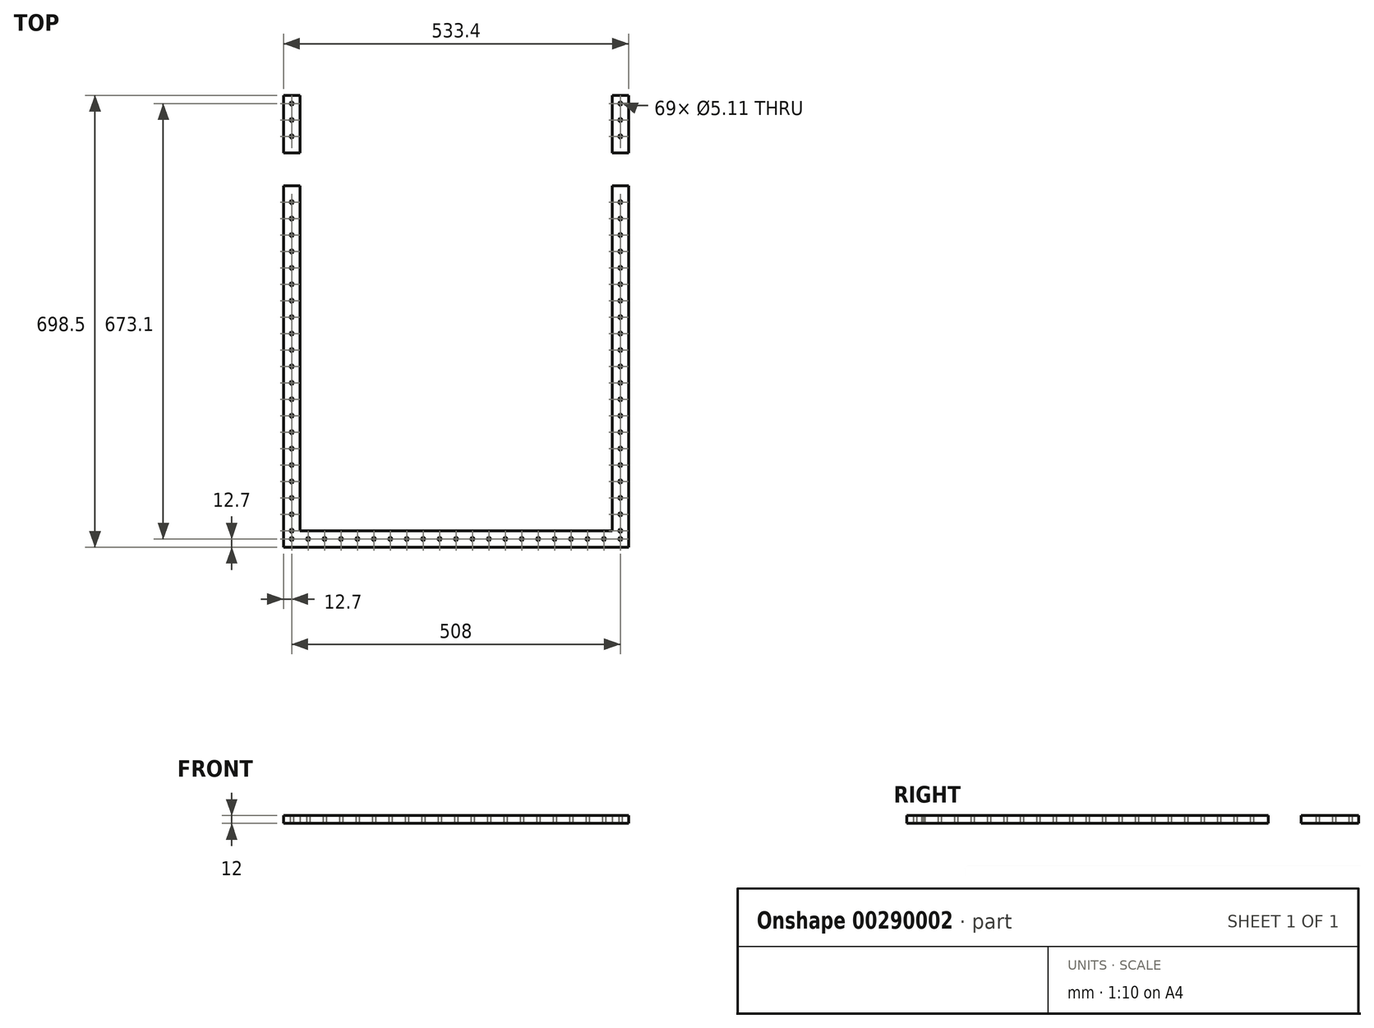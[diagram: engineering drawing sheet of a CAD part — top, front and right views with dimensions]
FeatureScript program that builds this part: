
annotation { "Feature Type Name" : "Feature", "Feature Type Description" : "" }
export const myFeature = defineFeature(function(context is Context, id is Id, definition is map)
    precondition{}
    {
        {
            var Q0;
            Q0=qCreatedBy(makeId("Top.planeOp"),FACE);
            var sketch = newSketch(context, id + "F0", { "sketchPlane" : qUnion([Q0])});
            skLineSegment(sketch, "E0.bottom", {"start": v(304.8, 0) * mm, "end": v(-304.8, 0) * mm, "construction": true});
            skLineSegment(sketch, "E0.top", {"start": v(304.8, 1066.8) * mm, "end": v(-304.8, 1066.8) * mm, "construction": true});
            skLineSegment(sketch, "E0.left", {"start": v(304.8, 0) * mm, "end": v(304.8, 1066.8) * mm, "construction": true});
            skLineSegment(sketch, "E0.right", {"start": v(-304.8, 0) * mm, "end": v(-304.8, 1066.8) * mm, "construction": true});
            skLineSegment(sketch, "E1.bottom", {"start": v(279.4, 965.2) * mm, "end": v(304.8, 965.2) * mm});
            skLineSegment(sketch, "E1.top", {"start": v(279.4, 914.4) * mm, "end": v(304.8, 914.4) * mm});
            skLineSegment(sketch, "E1.left", {"start": v(279.4, 965.2) * mm, "end": v(279.4, 914.4) * mm});
            skLineSegment(sketch, "E1.right", {"start": v(304.8, 965.2) * mm, "end": v(304.8, 914.4) * mm});
            skLineSegment(sketch, "E2.bottom", {"start": v(-279.4, 965.2) * mm, "end": v(-304.8, 965.2) * mm});
            skLineSegment(sketch, "E2.top", {"start": v(-279.4, 914.4) * mm, "end": v(-304.8, 914.4) * mm});
            skLineSegment(sketch, "E2.left", {"start": v(-279.4, 965.2) * mm, "end": v(-279.4, 914.4) * mm});
            skLineSegment(sketch, "E2.right", {"start": v(-304.8, 965.2) * mm, "end": v(-304.8, 914.4) * mm});
            skLineSegment(sketch, "E3.bottom", {"start": v(-214.63, 383.54) * mm, "end": v(214.63, 383.54) * mm, "construction": true});
            skLineSegment(sketch, "E3.top", {"start": v(-214.63, 1066.8) * mm, "end": v(214.63, 1066.8) * mm, "construction": true});
            skLineSegment(sketch, "E3.left", {"start": v(-214.63, 383.54) * mm, "end": v(-214.63, 1066.8) * mm, "construction": true});
            skLineSegment(sketch, "E3.right", {"start": v(214.63, 383.54) * mm, "end": v(214.63, 1066.8) * mm, "construction": true});
            skPoint(sketch, "E3.middle", {"position": v(0, 725.17) * mm});
            skLineSegment(sketch, "E4.bottom", {"start": v(25.4, 345.44) * mm, "end": v(-25.4, 345.44) * mm});
            skLineSegment(sketch, "E4.top", {"start": v(25.4, 320.04) * mm, "end": v(-25.4, 320.04) * mm});
            skLineSegment(sketch, "E4.left", {"start": v(25.4, 345.44) * mm, "end": v(25.4, 320.04) * mm});
            skLineSegment(sketch, "E4.right", {"start": v(-25.4, 345.44) * mm, "end": v(-25.4, 320.04) * mm});
            skPoint(sketch, "E4.middle", {"position": v(0, 332.74) * mm});
            skLineSegment(sketch, "E5", {"start": v(0, 1066.8) * mm, "end": v(0, 0) * mm, "construction": true});
            skLineSegment(sketch, "E6", {"start": v(-266.7, 1054.1) * mm, "end": v(-241.3, 1054.1) * mm});
            skLineSegment(sketch, "E7", {"start": v(-241.3, 1054.1) * mm, "end": v(-241.3, 965.2) * mm});
            skLineSegment(sketch, "E8", {"start": v(-266.7, 1054.1) * mm, "end": v(-266.7, 965.2) * mm});
            skLineSegment(sketch, "E9", {"start": v(-266.7, 914.4) * mm, "end": v(-266.7, 355.6) * mm});
            skLineSegment(sketch, "E10", {"start": v(-266.7, 355.6) * mm, "end": v(266.7, 355.6) * mm});
            skLineSegment(sketch, "E11", {"start": v(266.7, 355.6) * mm, "end": v(266.7, 914.4) * mm});
            skLineSegment(sketch, "E12", {"start": v(266.7, 965.2) * mm, "end": v(266.7, 1054.1) * mm});
            skLineSegment(sketch, "E13", {"start": v(266.7, 1054.1) * mm, "end": v(241.3, 1054.1) * mm});
            skLineSegment(sketch, "E14", {"start": v(241.3, 1054.1) * mm, "end": v(241.3, 965.2) * mm});
            skLineSegment(sketch, "E15", {"start": v(241.3, 914.4) * mm, "end": v(241.3, 381) * mm});
            skLineSegment(sketch, "E16", {"start": v(241.3, 381) * mm, "end": v(-241.3, 381) * mm});
            skLineSegment(sketch, "E17", {"start": v(-241.3, 914.4) * mm, "end": v(-241.3, 381) * mm});
            skPoint(sketch, "E17.startSnap0", {"position": v(-292.1, 914.4) * mm});
            skPoint(sketch, "E18", {"position": v(0, 355.6) * mm});
            skCircle(sketch, "E19", {"center": v(-254, 1041.4) * mm, "radius": 2.55 * mm});
            skCircle(sketch, "E20.0.1.0", {"center": v(-254, 1016) * mm, "radius": 2.55 * mm});
            skCircle(sketch, "E20.0.2.0", {"center": v(-254, 990.6) * mm, "radius": 2.55 * mm});
            skCircle(sketch, "E20.0.6.0", {"center": v(-254, 889) * mm, "radius": 2.55 * mm});
            skCircle(sketch, "E20.0.7.0", {"center": v(-254, 863.6) * mm, "radius": 2.55 * mm});
            skCircle(sketch, "E20.0.8.0", {"center": v(-254, 838.2) * mm, "radius": 2.55 * mm});
            skCircle(sketch, "E20.0.9.0", {"center": v(-254, 812.8) * mm, "radius": 2.55 * mm});
            skCircle(sketch, "E20.0.10.0", {"center": v(-254, 787.4) * mm, "radius": 2.55 * mm});
            skCircle(sketch, "E20.0.11.0", {"center": v(-254, 762) * mm, "radius": 2.55 * mm});
            skCircle(sketch, "E20.0.12.0", {"center": v(-254, 736.6) * mm, "radius": 2.55 * mm});
            skCircle(sketch, "E20.0.13.0", {"center": v(-254, 711.2) * mm, "radius": 2.55 * mm});
            skCircle(sketch, "E20.0.14.0", {"center": v(-254, 685.8) * mm, "radius": 2.55 * mm});
            skCircle(sketch, "E20.0.15.0", {"center": v(-254, 660.4) * mm, "radius": 2.55 * mm});
            skCircle(sketch, "E20.0.16.0", {"center": v(-254, 635) * mm, "radius": 2.55 * mm});
            skCircle(sketch, "E20.0.17.0", {"center": v(-254, 609.6) * mm, "radius": 2.55 * mm});
            skCircle(sketch, "E20.0.18.0", {"center": v(-254, 584.2) * mm, "radius": 2.55 * mm});
            skCircle(sketch, "E20.0.19.0", {"center": v(-254, 558.8) * mm, "radius": 2.55 * mm});
            skCircle(sketch, "E20.0.20.0", {"center": v(-254, 533.4) * mm, "radius": 2.55 * mm});
            skCircle(sketch, "E20.0.21.0", {"center": v(-254, 508) * mm, "radius": 2.55 * mm});
            skCircle(sketch, "E20.0.22.0", {"center": v(-254, 482.6) * mm, "radius": 2.55 * mm});
            skCircle(sketch, "E20.0.23.0", {"center": v(-254, 457.2) * mm, "radius": 2.55 * mm});
            skCircle(sketch, "E20.0.24.0", {"center": v(-254, 431.8) * mm, "radius": 2.55 * mm});
            skCircle(sketch, "E20.0.25.0", {"center": v(-254, 406.4) * mm, "radius": 2.55 * mm});
            skCircle(sketch, "E20.0.26.0", {"center": v(-254, 381) * mm, "radius": 2.55 * mm});
            skCircle(sketch, "E20.1.0.0", {"center": v(254, 1041.4) * mm, "radius": 2.55 * mm});
            skCircle(sketch, "E20.1.1.0", {"center": v(254, 1016) * mm, "radius": 2.55 * mm});
            skCircle(sketch, "E20.1.2.0", {"center": v(254, 990.6) * mm, "radius": 2.55 * mm});
            skCircle(sketch, "E20.1.6.0", {"center": v(254, 889) * mm, "radius": 2.55 * mm});
            skCircle(sketch, "E20.1.7.0", {"center": v(254, 863.6) * mm, "radius": 2.55 * mm});
            skCircle(sketch, "E20.1.8.0", {"center": v(254, 838.2) * mm, "radius": 2.55 * mm});
            skCircle(sketch, "E20.1.9.0", {"center": v(254, 812.8) * mm, "radius": 2.55 * mm});
            skCircle(sketch, "E20.1.10.0", {"center": v(254, 787.4) * mm, "radius": 2.55 * mm});
            skCircle(sketch, "E20.1.11.0", {"center": v(254, 762) * mm, "radius": 2.55 * mm});
            skCircle(sketch, "E20.1.12.0", {"center": v(254, 736.6) * mm, "radius": 2.55 * mm});
            skCircle(sketch, "E20.1.13.0", {"center": v(254, 711.2) * mm, "radius": 2.55 * mm});
            skCircle(sketch, "E20.1.14.0", {"center": v(254, 685.8) * mm, "radius": 2.55 * mm});
            skCircle(sketch, "E20.1.15.0", {"center": v(254, 660.4) * mm, "radius": 2.55 * mm});
            skCircle(sketch, "E20.1.16.0", {"center": v(254, 635) * mm, "radius": 2.55 * mm});
            skCircle(sketch, "E20.1.17.0", {"center": v(254, 609.6) * mm, "radius": 2.55 * mm});
            skCircle(sketch, "E20.1.18.0", {"center": v(254, 584.2) * mm, "radius": 2.55 * mm});
            skCircle(sketch, "E20.1.19.0", {"center": v(254, 558.8) * mm, "radius": 2.55 * mm});
            skCircle(sketch, "E20.1.20.0", {"center": v(254, 533.4) * mm, "radius": 2.55 * mm});
            skCircle(sketch, "E20.1.21.0", {"center": v(254, 508) * mm, "radius": 2.55 * mm});
            skCircle(sketch, "E20.1.22.0", {"center": v(254, 482.6) * mm, "radius": 2.55 * mm});
            skCircle(sketch, "E20.1.23.0", {"center": v(254, 457.2) * mm, "radius": 2.55 * mm});
            skCircle(sketch, "E20.1.24.0", {"center": v(254, 431.8) * mm, "radius": 2.55 * mm});
            skCircle(sketch, "E20.1.25.0", {"center": v(254, 406.4) * mm, "radius": 2.55 * mm});
            skCircle(sketch, "E20.1.26.0", {"center": v(254, 381) * mm, "radius": 2.55 * mm});
            skLineSegment(sketch, "E20.direction1", {"start": v(-254, 1041.4) * mm, "end": v(254, 1041.4) * mm, "construction": true});
            skLineSegment(sketch, "E20.direction2", {"start": v(-254, 1041.4) * mm, "end": v(-254, 1016) * mm, "construction": true});
            skCircle(sketch, "E21", {"center": v(-254, 368.3) * mm, "radius": 2.55 * mm});
            skCircle(sketch, "E22.1.0.0", {"center": v(-228.6, 368.3) * mm, "radius": 2.55 * mm});
            skCircle(sketch, "E22.2.0.0", {"center": v(-203.2, 368.3) * mm, "radius": 2.55 * mm});
            skCircle(sketch, "E22.3.0.0", {"center": v(-177.8, 368.3) * mm, "radius": 2.55 * mm});
            skCircle(sketch, "E22.4.0.0", {"center": v(-152.4, 368.3) * mm, "radius": 2.55 * mm});
            skCircle(sketch, "E22.5.0.0", {"center": v(-127, 368.3) * mm, "radius": 2.55 * mm});
            skCircle(sketch, "E22.6.0.0", {"center": v(-101.6, 368.3) * mm, "radius": 2.55 * mm});
            skCircle(sketch, "E22.7.0.0", {"center": v(-76.2, 368.3) * mm, "radius": 2.55 * mm});
            skCircle(sketch, "E22.8.0.0", {"center": v(-50.8, 368.3) * mm, "radius": 2.55 * mm});
            skCircle(sketch, "E22.9.0.0", {"center": v(-25.4, 368.3) * mm, "radius": 2.55 * mm});
            skCircle(sketch, "E22.10.0.0", {"center": v(0, 368.3) * mm, "radius": 2.55 * mm});
            skCircle(sketch, "E22.11.0.0", {"center": v(25.4, 368.3) * mm, "radius": 2.55 * mm});
            skCircle(sketch, "E22.12.0.0", {"center": v(50.8, 368.3) * mm, "radius": 2.55 * mm});
            skCircle(sketch, "E22.13.0.0", {"center": v(76.2, 368.3) * mm, "radius": 2.55 * mm});
            skCircle(sketch, "E22.14.0.0", {"center": v(101.6, 368.3) * mm, "radius": 2.55 * mm});
            skCircle(sketch, "E22.15.0.0", {"center": v(127, 368.3) * mm, "radius": 2.55 * mm});
            skCircle(sketch, "E22.16.0.0", {"center": v(152.4, 368.3) * mm, "radius": 2.55 * mm});
            skCircle(sketch, "E22.17.0.0", {"center": v(177.8, 368.3) * mm, "radius": 2.55 * mm});
            skCircle(sketch, "E22.18.0.0", {"center": v(203.2, 368.3) * mm, "radius": 2.55 * mm});
            skCircle(sketch, "E22.19.0.0", {"center": v(228.6, 368.3) * mm, "radius": 2.55 * mm});
            skLineSegment(sketch, "E22.direction1", {"start": v(-254, 368.3) * mm, "end": v(-228.6, 368.3) * mm, "construction": true});
            skCircle(sketch, "E23.0.20.0", {"center": v(254, 368.3) * mm, "radius": 2.55 * mm});
            skLineSegment(sketch, "E24", {"start": v(-266.7, 965.2) * mm, "end": v(-241.3, 965.2) * mm});
            skLineSegment(sketch, "E25", {"start": v(-241.3, 914.4) * mm, "end": v(-266.7, 914.4) * mm});
            skLineSegment(sketch, "E26", {"start": v(241.3, 914.4) * mm, "end": v(266.7, 914.4) * mm});
            skLineSegment(sketch, "E27", {"start": v(266.7, 965.2) * mm, "end": v(241.3, 965.2) * mm});
            skSolve(sketch);
        }
        {
            var Q0;
            Q0=makeQuery(id+"F0.imprint","IMPRINT",FACE,{"disambiguationData":[TD([[makeQuery(id+"F0.imprint","IMPRINT",EDGE,{"derivedFrom":sQuery(id+"F0.wireOp",EDGE,"E6")}),-1.0]])]});
            var Q1;
            Q1=makeQuery(id+"F0.imprint","IMPRINT",FACE,{"disambiguationData":[TD([[makeQuery(id+"F0.imprint","IMPRINT",EDGE,{"derivedFrom":sQuery(id+"F0.wireOp",EDGE,"E12")}),1.0]])]});
            var Q2;
            Q2=makeQuery(id+"F0.imprint","IMPRINT",FACE,{"disambiguationData":[TD([[makeQuery(id+"F0.imprint","IMPRINT",EDGE,{"derivedFrom":sQuery(id+"F0.wireOp",EDGE,"E9")}),1.0]])]});
            extrude(context, id + "F1", {"entities" : qUnion([Q0, Q1, Q2]), "depth" : 12 * mm});
        }
    });
